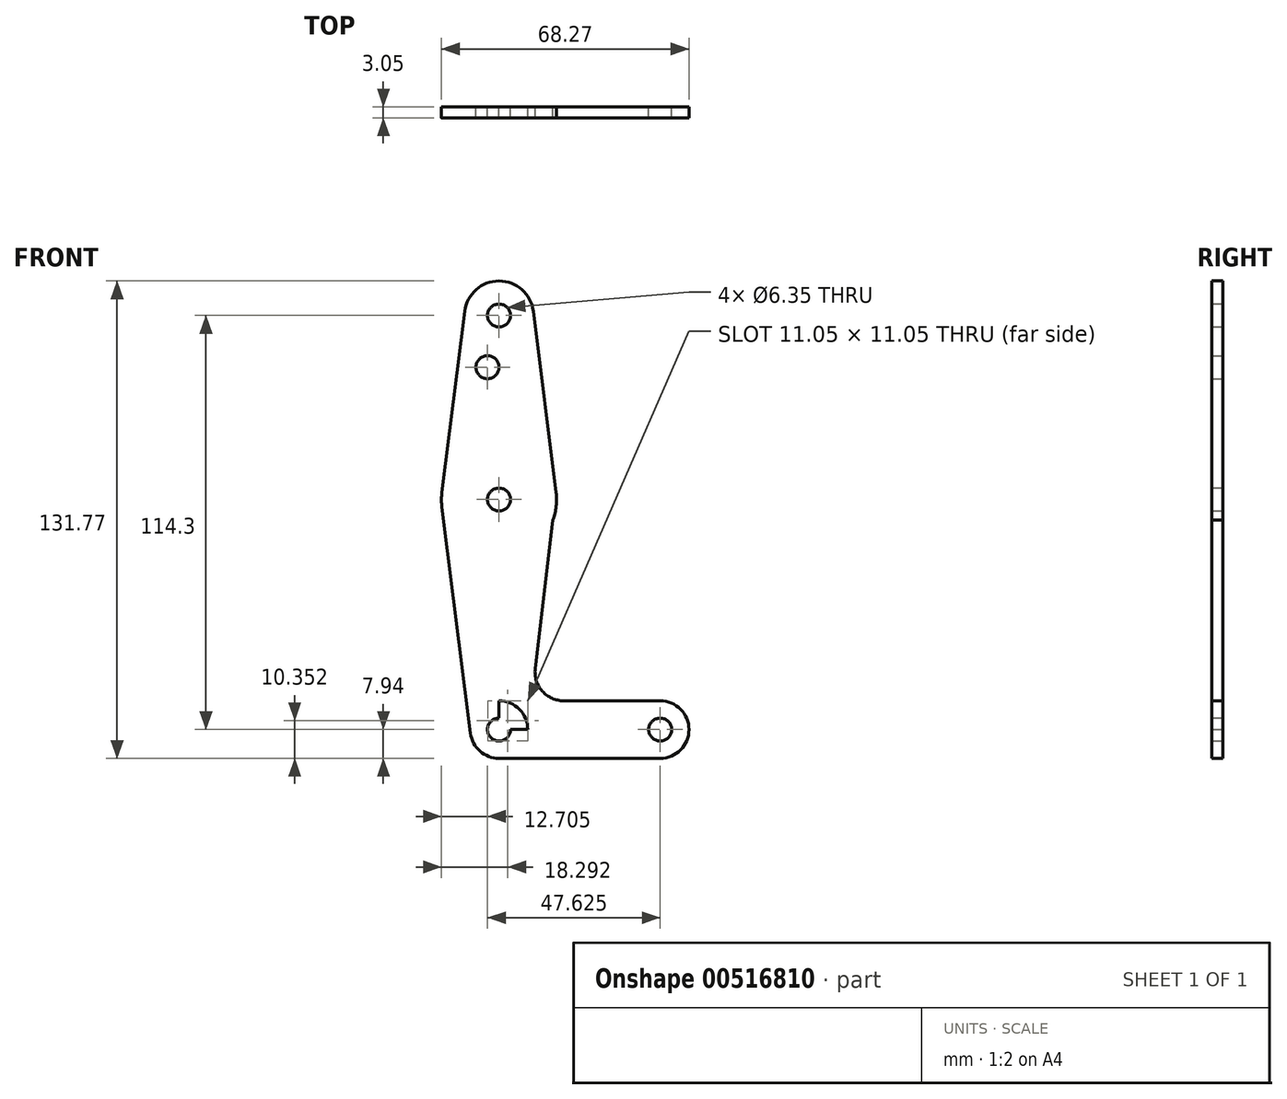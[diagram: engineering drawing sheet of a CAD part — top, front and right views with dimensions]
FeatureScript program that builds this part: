
annotation { "Feature Type Name" : "Feature", "Feature Type Description" : "" }
export const myFeature = defineFeature(function(context is Context, id is Id, definition is map)
    precondition{}
    {
        {
            var Q0;
            Q0=qCreatedBy(makeId("Front.planeOp"),FACE);
            var sketch = newSketch(context, id + "F0", { "sketchPlane" : qUnion([Q0])});
            skCircle(sketch, "E0", {"center": v(0, 0) * mm, "radius": 7.94 * mm});
            skCircle(sketch, "E1", {"center": v(0, 63.5) * mm, "radius": 15.88 * mm});
            skCircle(sketch, "E2", {"center": v(0, 114.3) * mm, "radius": 9.53 * mm});
            skCircle(sketch, "E3", {"center": v(44.45, 0) * mm, "radius": 7.94 * mm});
            skLineSegment(sketch, "E4", {"start": v(0, 114.3) * mm, "end": v(0, 0) * mm});
            skLineSegment(sketch, "E5", {"start": v(0, 0) * mm, "end": v(44.45, 0) * mm});
            skLineSegment(sketch, "E6", {"start": v(0, 63.5) * mm, "end": v(0, 0) * mm});
            skLineSegment(sketch, "E7", {"start": v(0, -7.94) * mm, "end": v(44.45, -7.94) * mm});
            skLineSegment(sketch, "E8", {"start": v(17.88, 7.94) * mm, "end": v(44.45, 7.94) * mm});
            skLineSegment(sketch, "E9", {"start": v(-9.45, 115.5) * mm, "end": v(-15.75, 65.48) * mm});
            skLineSegment(sketch, "E10", {"start": v(9.45, 115.5) * mm, "end": v(15.75, 65.48) * mm});
            skLineSegment(sketch, "E11", {"start": v(15.75, 65.48) * mm, "end": v(9.99, 16.82) * mm});
            skCircle(sketch, "E12", {"center": v(0, 114.3) * mm, "radius": 0.32 * mm});
            skCircle(sketch, "E13", {"center": v(-3.17, 100.03) * mm, "radius": 3.18 * mm});
            skCircle(sketch, "E14", {"center": v(0, 63.5) * mm, "radius": 3.17 * mm});
            skCircle(sketch, "E15", {"center": v(0, 0) * mm, "radius": 3.18 * mm});
            skCircle(sketch, "E16", {"center": v(44.45, 0) * mm, "radius": 3.18 * mm});
            skCircle(sketch, "E17", {"center": v(0, 114.3) * mm, "radius": 3.18 * mm});
            skArc(sketch, "E18.filletArc", {"start": v(9.99, 16.82) * mm, "mid": v(11.94, 10.6) * mm, "end": v(17.88, 7.94) * mm});
            skLineSegment(sketch, "E19", {"start": v(-15.73, 61.37) * mm, "end": v(-7.88, -1) * mm});
            skSolve(sketch);
        }
        {
            var Q0;
            Q0=qSketchRegion(id+"F0",true);
            var Q1;
            {var subQ0=sQuery(id+"F0.wireOp",EDGE,"E6");var subQ3=sQuery(id+"F0.wireOp",EDGE,"E0");var subQ4=makeQuery(id+"F0.imprint","INTERSECT",VERTEX,{"derivedFrom":[subQ3,subQ0]});Q1=makeQuery(id+"F0.imprint","IMPRINT",FACE,{"disambiguationData":[TD([[makeQuery(id+"F0.imprint","IMPRINT",EDGE,{"disambiguationData":[TD([[subQ4,1.0]])],"derivedFrom":subQ3}),1.0]])]});}
            extrude(context, id + "F1", {"entities" : qUnion([Q0, Q1]), "depth" : 3.05 * mm});
        }
    });
